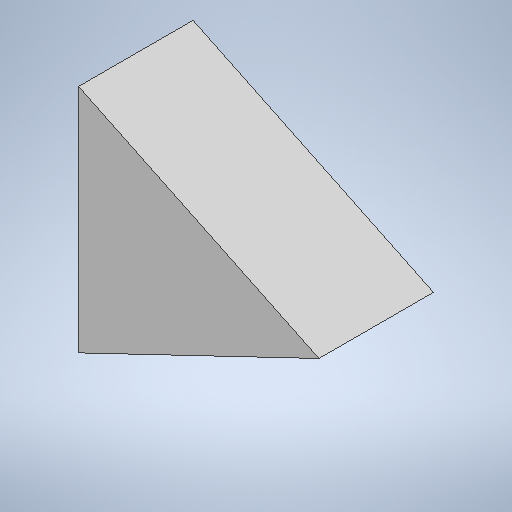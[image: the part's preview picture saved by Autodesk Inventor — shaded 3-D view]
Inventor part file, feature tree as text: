
AUTODESK INVENTOR PART (.ipt)
format: ipt  version: 2025.1 (Build 291241000, 241)  size: 192,000 bytes
history: native  units: mm
features: extrude x1, sketch x1
ambient origin geometry x8: Origin, YZ Plane, XZ Plane, XY Plane, X Axis, Y Axis, Z Axis, Center Point
bodies: Solid1 (feature_tree)
feature tree (2):
  extrude  "Extrusion1"  Depth=10.0mm
  sketch  "Sketch1"  dims[d0=21.0mm d1=10.0755mm d2=10.0755mm d3=10.0mm d4=0.0mm]
